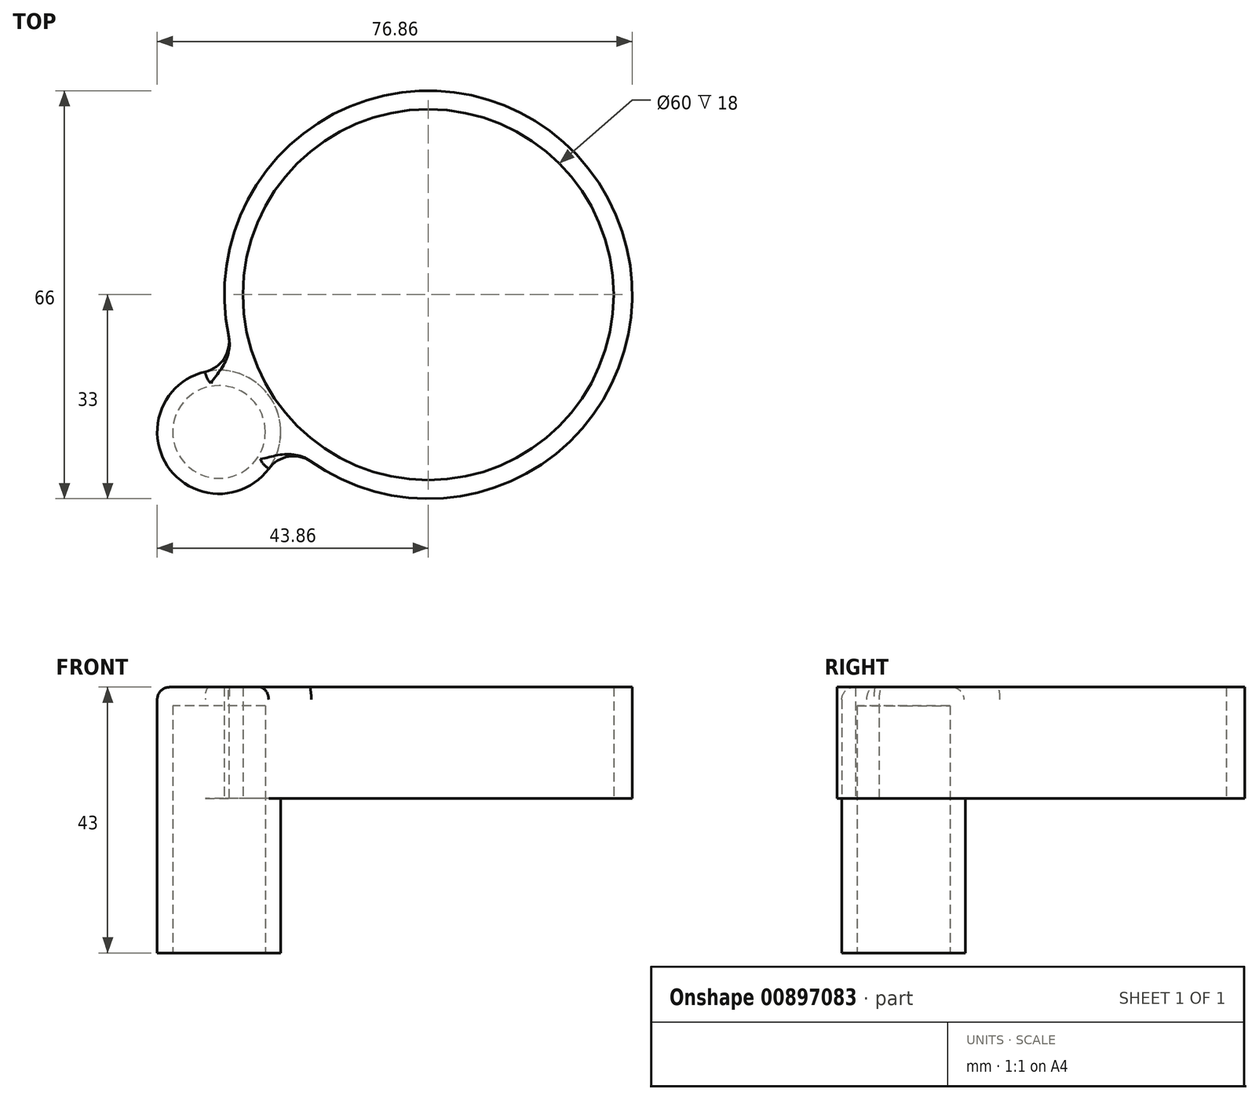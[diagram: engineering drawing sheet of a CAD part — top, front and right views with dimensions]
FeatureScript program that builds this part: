
annotation { "Feature Type Name" : "Feature", "Feature Type Description" : "" }
export const myFeature = defineFeature(function(context is Context, id is Id, definition is map)
    precondition{}
    {
        {
            var Q0;
            Q0=qCreatedBy(makeId("Top.planeOp"),FACE);
            var sketch = newSketch(context, id + "F0", { "sketchPlane" : qUnion([Q0])});
            skCircle(sketch, "E0", {"center": v(0, 0) * mm, "radius": 30 * mm});
            skCircle(sketch, "E1.0", {"center": v(0, 0) * mm, "radius": 33 * mm});
            skCircle(sketch, "E2", {"center": v(-33.86, -22.21) * mm, "radius": 7.5 * mm});
            skCircle(sketch, "E3.0", {"center": v(-33.86, -22.21) * mm, "radius": 10 * mm});
            skSolve(sketch);
        }
        {
            var Q0;
            Q0=makeQuery(id+"F0.imprint","IMPRINT",FACE,{"disambiguationData":[TD([[makeQuery(id+"F0.imprint","IMPRINT",EDGE,{"derivedFrom":sQuery(id+"F0.wireOp",EDGE,"E0")}),-1.0]])]});
            var Q1;
            Q1=makeQuery(id+"F0.imprint","IMPRINT",FACE,{"disambiguationData":[TD([[makeQuery(id+"F0.imprint","IMPRINT",EDGE,{"derivedFrom":sQuery(id+"F0.wireOp",EDGE,"E2")}),1.0]])]});
            var Q2;
            {var subQ0=sQuery(id+"F0.wireOp",EDGE,"E1.0");var subQ1=makeQuery(id+"F0.imprint","INTERSECT",VERTEX,{"derivedFrom":[subQ0,sQuery(id+"F0.wireOp",EDGE,"E2")]});Q2=makeQuery(id+"F0.imprint","IMPRINT",FACE,{"disambiguationData":[TD([[makeQuery(id+"F0.imprint","IMPRINT",EDGE,{"disambiguationData":[TD([[subQ1,1.0]])],"derivedFrom":subQ0}),1.0]])]});}
            var Q3;
            {var subQ0=sQuery(id+"F0.wireOp",EDGE,"E2");Q3=makeQuery(id+"F0.imprint","IMPRINT",FACE,{"disambiguationData":[TD([[makeQuery(id+"F0.imprint","IMPRINT",EDGE,{"derivedFrom":subQ0}),-1.0]])]});}
            extrude(context, id + "F1", {"entities" : qUnion([Q0, Q1, Q2, Q3]), "depth" : 18 * mm, "offsetDistance" : 25 * mm});
        }
        {
            var Q0;
            Q0=makeQuery(id+"F0.imprint","IMPRINT",FACE,{"disambiguationData":[TD([[makeQuery(id+"F0.imprint","IMPRINT",EDGE,{"derivedFrom":sQuery(id+"F0.wireOp",EDGE,"E2")}),1.0]])]});
            extrude(context, id + "F2", {"entities" : qUnion([Q0]), "operationType" : NewBodyOperationType.REMOVE, "depth" : 15 * mm, "offsetDistance" : 25 * mm});
        }
        {
            var Q0;
            {var subQ0=sQuery(id+"F0.wireOp",EDGE,"E1.0");var subQ1=makeQuery(id+"F0.imprint","INTERSECT",VERTEX,{"derivedFrom":[subQ0,sQuery(id+"F0.wireOp",EDGE,"E2")]});Q0=makeQuery(id+"F0.imprint","IMPRINT",FACE,{"disambiguationData":[TD([[makeQuery(id+"F0.imprint","IMPRINT",EDGE,{"disambiguationData":[TD([[subQ1,1.0]])],"derivedFrom":subQ0}),1.0]])]});}
            var Q1;
            {var subQ0=sQuery(id+"F0.wireOp",EDGE,"E2");Q1=makeQuery(id+"F0.imprint","IMPRINT",FACE,{"disambiguationData":[TD([[makeQuery(id+"F0.imprint","IMPRINT",EDGE,{"derivedFrom":subQ0}),-1.0]])]});}
            extrude(context, id + "F3", {"entities" : qUnion([Q0, Q1]), "operationType" : NewBodyOperationType.ADD, "oppositeDirection" : true, "depth" : 25 * mm, "offsetDistance" : 25 * mm});
        }
        {
            var Q0;
            Q0=makeQuery(id+"F1.opExtrude","CAP_EDGE",EDGE,{"disambiguationData":[OSD([sQuery(id+"F0.wireOp",EDGE,"E3.0")])],"isStart":false});
            fillet(context, id + "F4", {"entities" : qUnion([Q0]), "radius" : 2 * mm, "tangentPropagation" : true, "allowEdgeOverflow" : false});
        }
        {
            var Q0;
            {var subQ0=sQuery(id+"F0.wireOp",EDGE,"E3.0");var subQ1=sQuery(id+"F0.wireOp",EDGE,"E1.0");Q0=makeQuery(id+"F1.opExtrude","SWEPT_EDGE",EDGE,{"disambiguationData":[OSD([subQ1,subQ0]),TDD([makeQuery(id+"F0.imprint","INTERSECT",VERTEX,{"disambiguationData":[OD(1.0)],"derivedFrom":[subQ1,subQ0]})])]});}
            var Q1;
            {var subQ0=sQuery(id+"F0.wireOp",EDGE,"E3.0");var subQ1=sQuery(id+"F0.wireOp",EDGE,"E1.0");Q1=makeQuery(id+"F1.opExtrude","SWEPT_EDGE",EDGE,{"disambiguationData":[OSD([subQ1,subQ0]),TDD([makeQuery(id+"F0.imprint","INTERSECT",VERTEX,{"disambiguationData":[OD(0.0)],"derivedFrom":[subQ1,subQ0]})])]});}
            fillet(context, id + "F5", {"entities" : qUnion([Q0, Q1]), "radius" : 5 * mm, "tangentPropagation" : true, "allowEdgeOverflow" : false});
        }
    });
